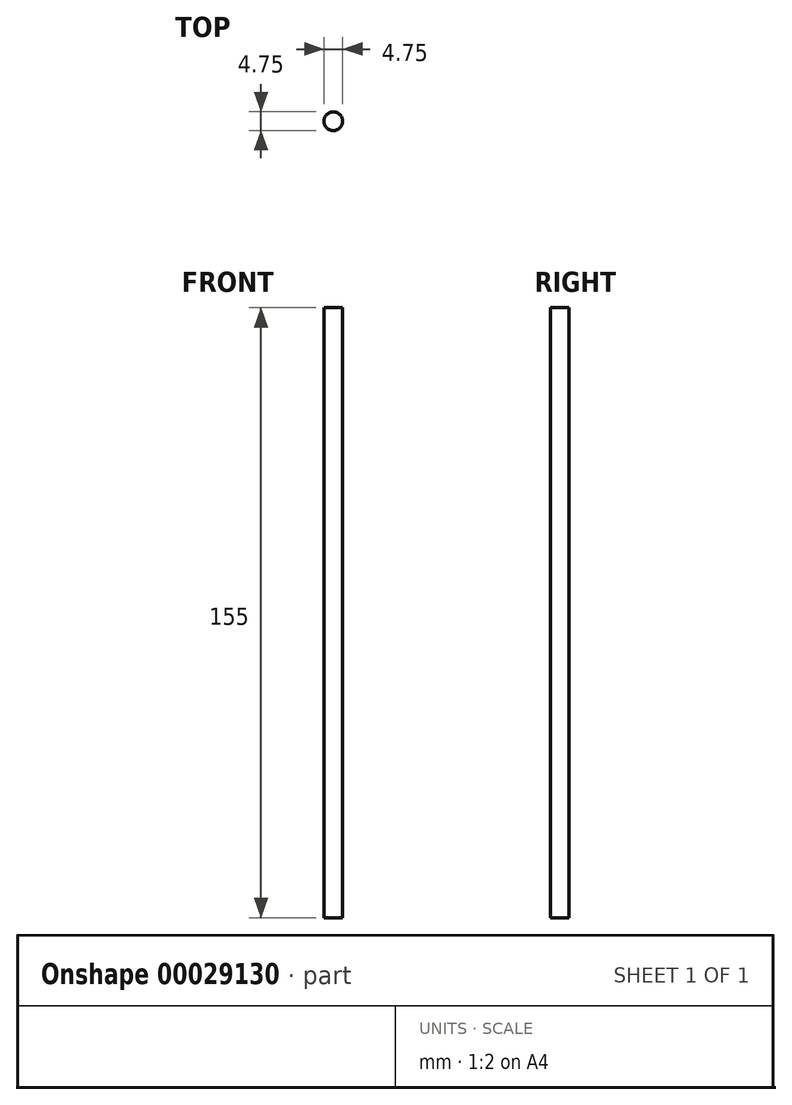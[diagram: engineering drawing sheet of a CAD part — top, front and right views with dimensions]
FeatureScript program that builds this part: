
annotation { "Feature Type Name" : "Feature", "Feature Type Description" : "" }
export const myFeature = defineFeature(function(context is Context, id is Id, definition is map)
    precondition{}
    {
        {
            var Q0;
            Q0=qCreatedBy(makeId("Top.planeOp"),FACE);
            var sketch = newSketch(context, id + "F0", { "sketchPlane" : qUnion([Q0])});
            skCircle(sketch, "E0", {"center": v(-50.14, -14.3) * mm, "radius": 2.38 * mm});
            skSolve(sketch);
        }
        {
            var Q0;
            Q0=qSketchRegion(id+"F0",true);
            extrude(context, id + "F1", {"entities" : qUnion([Q0]), "oppositeDirection" : true, "depth" : 155 * mm});
        }
    });
